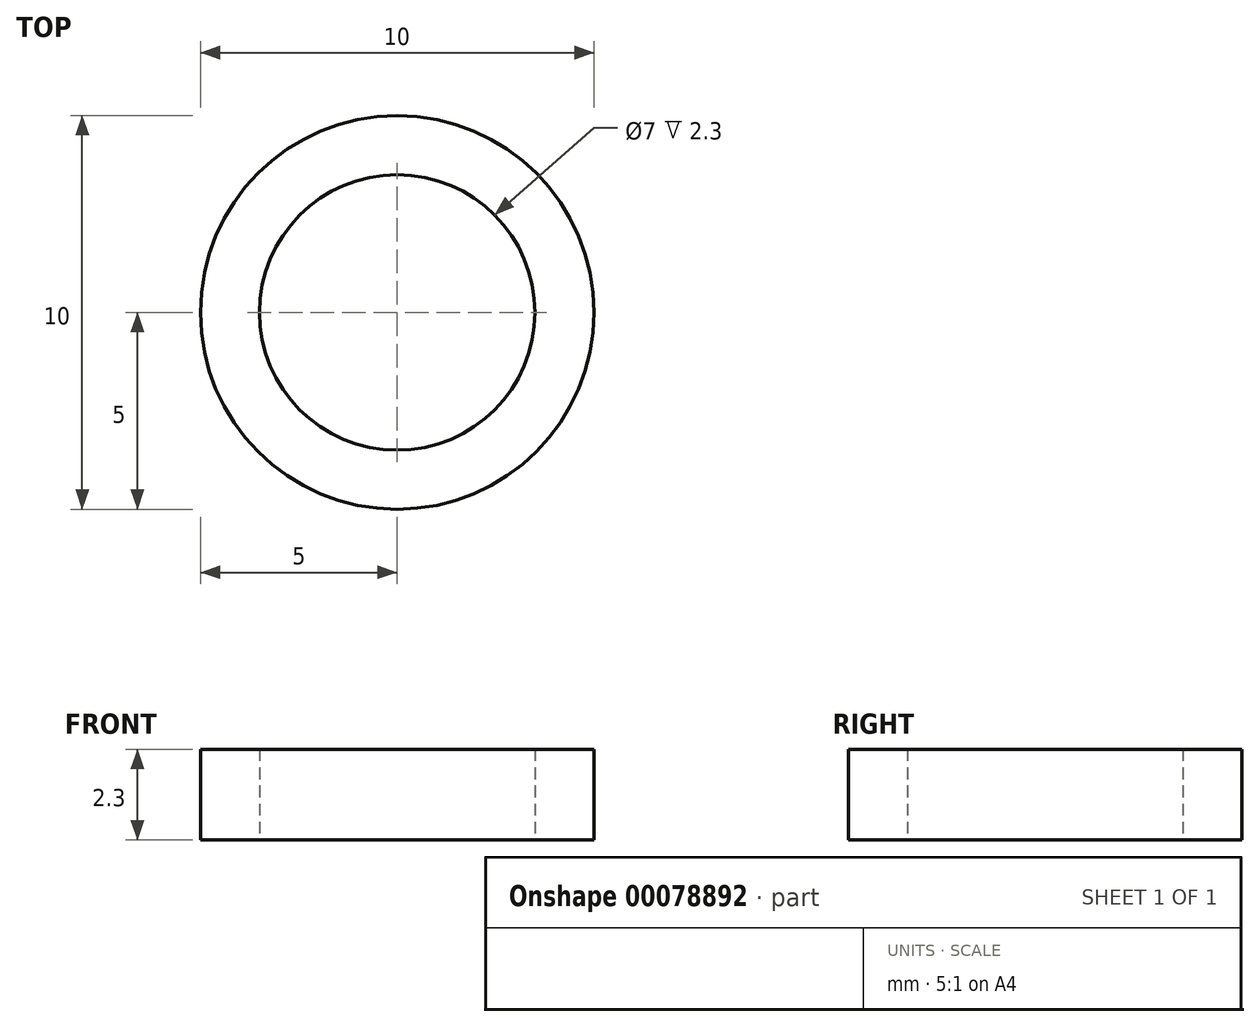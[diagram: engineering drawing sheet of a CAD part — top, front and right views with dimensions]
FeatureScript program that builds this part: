
annotation { "Feature Type Name" : "Feature", "Feature Type Description" : "" }
export const myFeature = defineFeature(function(context is Context, id is Id, definition is map)
    precondition{}
    {
        {
            var Q0;
            Q0=qCreatedBy(makeId("Top.planeOp"),FACE);
            var sketch = newSketch(context, id + "F0", { "sketchPlane" : qUnion([Q0])});
            skCircle(sketch, "E0", {"center": v(0, 0) * mm, "radius": 5 * mm});
            skCircle(sketch, "E1", {"center": v(0, 0) * mm, "radius": 3.5 * mm});
            skSolve(sketch);
        }
        {
            var Q0;
            Q0=makeQuery(id+"F0.imprint","IMPRINT",FACE,{"disambiguationData":[TD([[makeQuery(id+"F0.imprint","IMPRINT",EDGE,{"derivedFrom":sQuery(id+"F0.wireOp",EDGE,"E0")}),1.0]])]});
            extrude(context, id + "F1", {"entities" : qUnion([Q0]), "depth" : 2.3 * mm});
        }
    });
